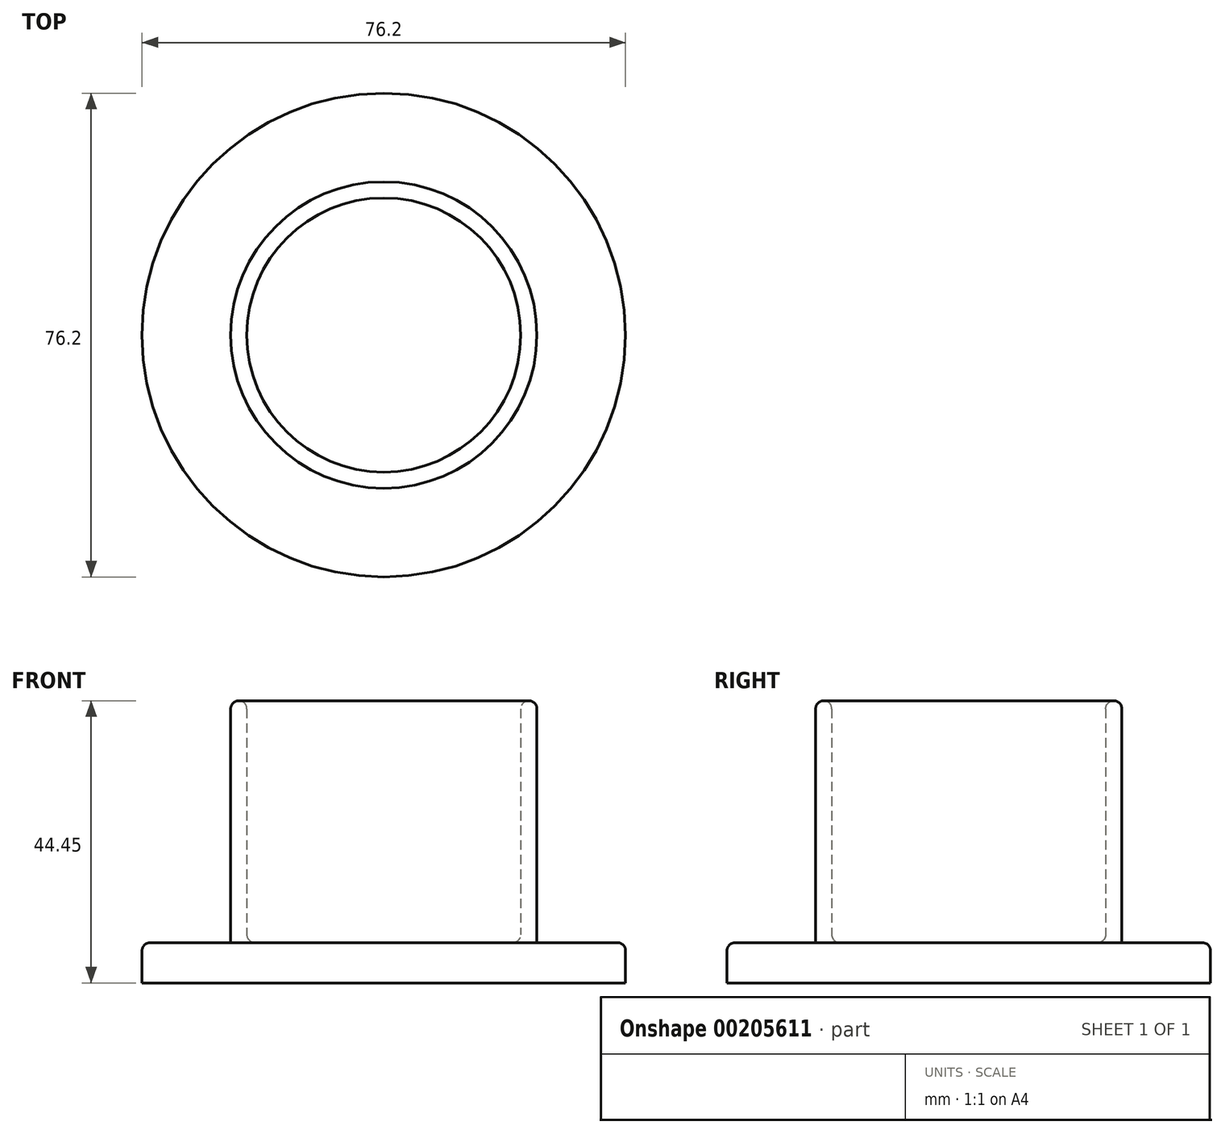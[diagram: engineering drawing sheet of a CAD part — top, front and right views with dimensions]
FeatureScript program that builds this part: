
annotation { "Feature Type Name" : "Feature", "Feature Type Description" : "" }
export const myFeature = defineFeature(function(context is Context, id is Id, definition is map)
    precondition{}
    {
        {
            var Q0;
            Q0=qCreatedBy(makeId("Top.planeOp"),FACE);
            var sketch = newSketch(context, id + "F0", { "sketchPlane" : qUnion([Q0])});
            skCircle(sketch, "E0", {"center": v(0, 0) * mm, "radius": 38.1 * mm});
            skSolve(sketch);
        }
        {
            var Q0;
            Q0 = qSketchRegion(id + "F0", true);
            extrude(context, id + "F1", {"entities" : qUnion([Q0]), "depth" : 6.35 * mm});
        }
        {
            var Q0;
            Q0=makeQuery(id+"F1.opExtrude","CAP_FACE",FACE,{"disambiguationData":[OSD([sQuery(id+"F0.wireOp",EDGE,"E0")])],"isStart":false});
            var sketch = newSketch(context, id + "F2", { "sketchPlane" : qUnion([Q0])});
            skCircle(sketch, "E1", {"center": v(0, 0) * mm, "radius": 24.13 * mm});
            skCircle(sketch, "E2", {"center": v(0, 0) * mm, "radius": 21.59 * mm});
            skSolve(sketch);
        }
        {
            var Q0;
            Q0=makeQuery(id+"F2.imprint","IMPRINT",FACE,{"disambiguationData":[TD([[makeQuery(id+"F2.imprint","IMPRINT",EDGE,{"derivedFrom":sQuery(id+"F2.wireOp",EDGE,"E1")}),1.0]])]});
            extrude(context, id + "F3", {"entities" : qUnion([Q0]), "operationType" : NewBodyOperationType.ADD, "depth" : 38.1 * mm});
        }
        {
            var Q0;
            Q0=makeQuery(id+"F3.opExtrude","CAP_EDGE",EDGE,{"disambiguationData":[OSD([sQuery(id+"F2.wireOp",EDGE,"E2")])],"isStart":true});
            var Q1;
            Q1=makeQuery(id+"F3.opExtrude","CAP_EDGE",EDGE,{"disambiguationData":[OSD([sQuery(id+"F2.wireOp",EDGE,"E1")])],"isStart":true});
            var Q2;
            Q2=makeQuery(id+"F1.opExtrude","CAP_EDGE",EDGE,{"disambiguationData":[OSD([sQuery(id+"F0.wireOp",EDGE,"E0")])],"isStart":false});
            var Q3;
            Q3=makeQuery(id+"F3.opExtrude","CAP_EDGE",EDGE,{"disambiguationData":[OSD([sQuery(id+"F2.wireOp",EDGE,"E2")])],"isStart":false});
            var Q4;
            Q4=makeQuery(id+"F3.opExtrude","CAP_EDGE",EDGE,{"disambiguationData":[OSD([sQuery(id+"F2.wireOp",EDGE,"E1")])],"isStart":false});
            fillet(context, id + "F4", {"entities" : qUnion([Q0, Q1, Q2, Q3, Q4]), "radius" : 1.27 * mm, "tangentPropagation" : true, "allowEdgeOverflow" : false});
        }
    });
